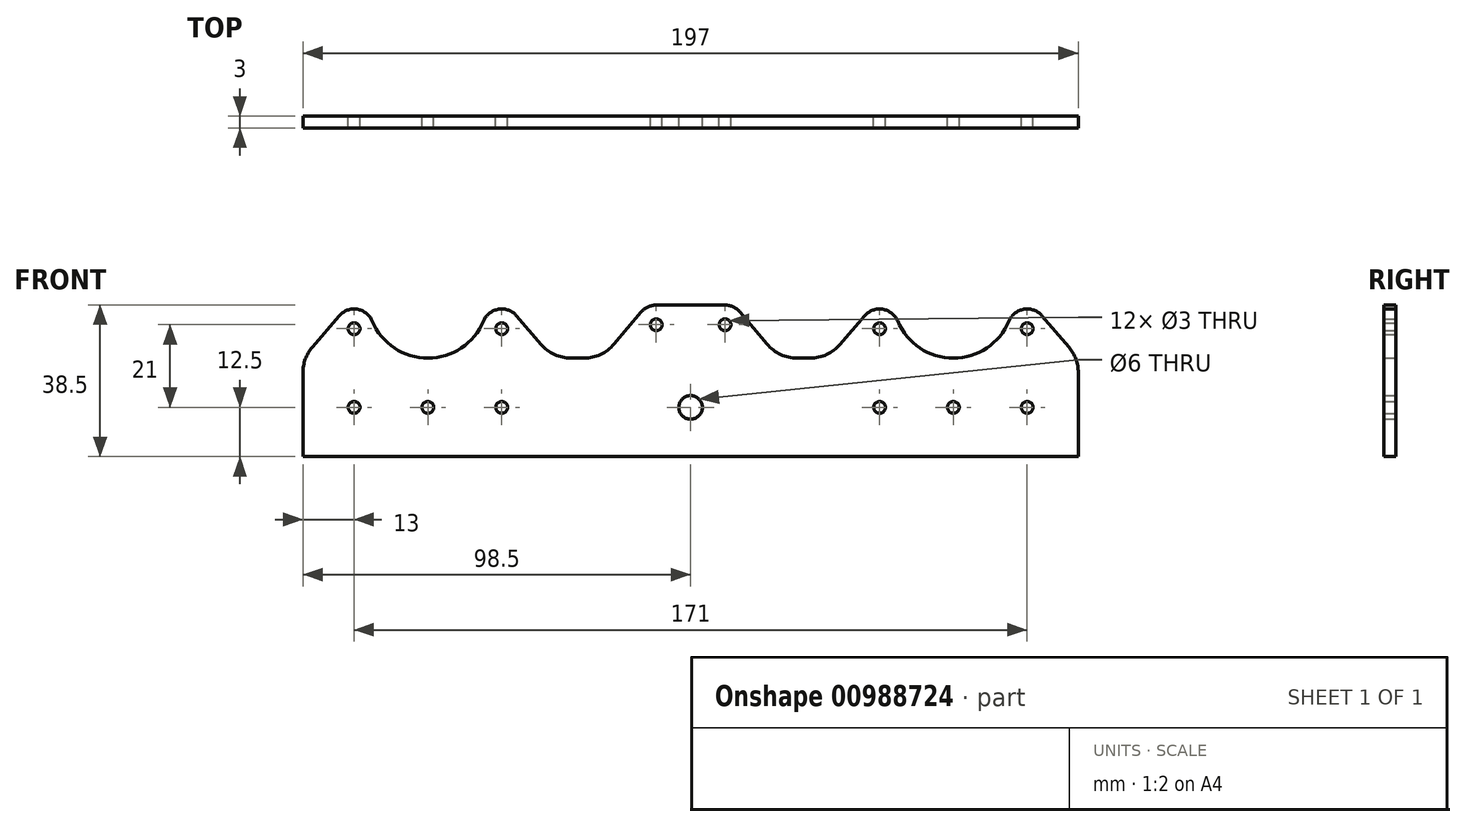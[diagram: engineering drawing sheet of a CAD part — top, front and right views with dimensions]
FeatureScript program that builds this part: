
annotation { "Feature Type Name" : "Feature", "Feature Type Description" : "" }
export const myFeature = defineFeature(function(context is Context, id is Id, definition is map)
    precondition{}
    {
        {
            var Q0;
            Q0=qCreatedBy(makeId("Front.planeOp"),FACE);
            var sketch = newSketch(context, id + "F0", { "sketchPlane" : qUnion([Q0])});
            skLineSegment(sketch, "E0.bottom", {"start": v(0, 0) * mm, "end": v(-197, 0) * mm});
            skLineSegment(sketch, "E0.top", {"start": v(0, 25) * mm, "end": v(-197, 25) * mm});
            skLineSegment(sketch, "E0.left", {"start": v(0, 0) * mm, "end": v(0, 25) * mm});
            skLineSegment(sketch, "E0.right", {"start": v(-197, 0) * mm, "end": v(-197, 25) * mm});
            skCircle(sketch, "E1", {"center": v(-13, 12.5) * mm, "radius": 1.5 * mm});
            skLineSegment(sketch, "E2", {"start": v(-197, 12.5) * mm, "end": v(0, 12.5) * mm, "construction": true});
            skCircle(sketch, "E3", {"center": v(-184, 12.5) * mm, "radius": 1.5 * mm});
            skCircle(sketch, "E4", {"center": v(-165.25, 12.5) * mm, "radius": 1.5 * mm});
            skCircle(sketch, "E5", {"center": v(-146.5, 12.5) * mm, "radius": 1.5 * mm});
            skCircle(sketch, "E6", {"center": v(-98.5, 12.5) * mm, "radius": 3 * mm});
            skCircle(sketch, "E7", {"center": v(-50.5, 12.5) * mm, "radius": 1.5 * mm});
            skCircle(sketch, "E8", {"center": v(-31.75, 12.5) * mm, "radius": 1.5 * mm});
            skCircle(sketch, "E9", {"center": v(-184, 12.5) * mm, "radius": 10 * mm, "construction": true});
            skCircle(sketch, "E10", {"center": v(-146.5, 12.5) * mm, "radius": 10 * mm, "construction": true});
            skCircle(sketch, "E11", {"center": v(-165.25, 12.5) * mm, "radius": 5.75 * mm, "construction": true});
            skCircle(sketch, "E12", {"center": v(-98.5, 12.5) * mm, "radius": 35 * mm, "construction": true});
            skCircle(sketch, "E13", {"center": v(-50.5, 12.5) * mm, "radius": 10 * mm, "construction": true});
            skCircle(sketch, "E14", {"center": v(-13, 12.5) * mm, "radius": 10 * mm, "construction": true});
            skCircle(sketch, "E15", {"center": v(-31.75, 12.5) * mm, "radius": 5.75 * mm, "construction": true});
            skCircle(sketch, "E16", {"center": v(-184, 32.5) * mm, "radius": 1.5 * mm});
            skCircle(sketch, "E17", {"center": v(-146.5, 32.5) * mm, "radius": 1.5 * mm});
            skCircle(sketch, "E18", {"center": v(-50.5, 32.5) * mm, "radius": 1.5 * mm});
            skCircle(sketch, "E19", {"center": v(-13, 32.5) * mm, "radius": 1.5 * mm});
            skLineSegment(sketch, "E20", {"start": v(0, 25) * mm, "end": v(-9.2, 35.75) * mm});
            skArc(sketch, "E21", {"start": v(-9.2, 35.75) * mm, "mid": v(-13.78, 37.44) * mm, "end": v(-17.62, 34.42) * mm});
            skArc(sketch, "E22", {"start": v(-45.88, 34.42) * mm, "mid": v(-49.72, 37.44) * mm, "end": v(-54.3, 35.75) * mm});
            skLineSegment(sketch, "E23", {"start": v(-54.3, 35.75) * mm, "end": v(-63.5, 25) * mm});
            skArc(sketch, "E24", {"start": v(-45.88, 34.42) * mm, "mid": v(-31.75, 25) * mm, "end": v(-17.62, 34.42) * mm});
            skLineSegment(sketch, "E25", {"start": v(-98.5, 0) * mm, "end": v(-98.5, 25) * mm, "construction": true});
            skArc(sketch, "E26.1.0.0", {"start": v(-179.38, 34.42) * mm, "mid": v(-165.25, 25) * mm, "end": v(-151.12, 34.42) * mm});
            skArc(sketch, "E26.1.0.1", {"start": v(-179.38, 34.42) * mm, "mid": v(-183.22, 37.44) * mm, "end": v(-187.8, 35.75) * mm});
            skLineSegment(sketch, "E26.1.0.2", {"start": v(-187.8, 35.75) * mm, "end": v(-197, 25) * mm});
            skLineSegment(sketch, "E26.1.0.3", {"start": v(-133.5, 25) * mm, "end": v(-142.7, 35.75) * mm});
            skArc(sketch, "E26.1.0.4", {"start": v(-142.7, 35.75) * mm, "mid": v(-147.28, 37.44) * mm, "end": v(-151.12, 34.42) * mm});
            skLineSegment(sketch, "E26.direction1", {"start": v(-45.88, 34.42) * mm, "end": v(-179.38, 34.42) * mm, "construction": true});
            skLineSegment(sketch, "E27", {"start": v(-98.5, 12.5) * mm, "end": v(-98.5, 33.5) * mm, "construction": true});
            skLineSegment(sketch, "E28", {"start": v(-107.25, 33.5) * mm, "end": v(-89.75, 33.5) * mm, "construction": true});
            skCircle(sketch, "E29", {"center": v(-107.25, 33.5) * mm, "radius": 1.5 * mm});
            skCircle(sketch, "E30", {"center": v(-89.75, 33.5) * mm, "radius": 1.5 * mm});
            skArc(sketch, "E31", {"start": v(-107.25, 38.5) * mm, "mid": v(-109.36, 38.03) * mm, "end": v(-111.08, 36.71) * mm});
            skArc(sketch, "E32", {"start": v(-85.92, 36.71) * mm, "mid": v(-87.64, 38.03) * mm, "end": v(-89.75, 38.5) * mm});
            skLineSegment(sketch, "E33", {"start": v(-107.25, 38.5) * mm, "end": v(-89.75, 38.5) * mm});
            skLineSegment(sketch, "E34", {"start": v(-85.92, 36.71) * mm, "end": v(-76.1, 25) * mm});
            skLineSegment(sketch, "E35", {"start": v(-111.08, 36.71) * mm, "end": v(-120.9, 25) * mm});
            skSolve(sketch);
        }
        {
            var Q0;
            Q0=makeQuery(id+"F0.imprint","IMPRINT",FACE,{"disambiguationData":[TD([[makeQuery(id+"F0.imprint","IMPRINT",EDGE,{"derivedFrom":sQuery(id+"F0.wireOp",EDGE,"E0.bottom")}),-1.0]])]});
            var Q1;
            Q1=makeQuery(id+"F0.imprint","IMPRINT",FACE,{"disambiguationData":[TD([[makeQuery(id+"F0.imprint","IMPRINT",EDGE,{"derivedFrom":sQuery(id+"F0.wireOp",EDGE,"E18")}),-1.0]])]});
            var Q2;
            {var subQ0=sQuery(id+"F0.wireOp",EDGE,"A3huXqgn-odZi-QKHd-XIsC-R8iYggHlKZpN");Q2=makeQuery(id+"F0.imprint","IMPRINT",FACE,{"disambiguationData":[TD([[makeQuery(id+"F0.imprint","IMPRINT",EDGE,{"derivedFrom":subQ0}),-1.0]])]});}
            var Q3;
            Q3=makeQuery(id+"F0.imprint","IMPRINT",FACE,{"disambiguationData":[TD([[makeQuery(id+"F0.imprint","IMPRINT",EDGE,{"derivedFrom":sQuery(id+"F0.wireOp",EDGE,"E19")}),-1.0]])]});
            var Q4;
            Q4=makeQuery(id+"F0.imprint","IMPRINT",FACE,{"disambiguationData":[TD([[makeQuery(id+"F0.imprint","IMPRINT",EDGE,{"derivedFrom":sQuery(id+"F0.wireOp",EDGE,"E16")}),-1.0]])]});
            var Q5;
            Q5=makeQuery(id+"F0.imprint","IMPRINT",FACE,{"disambiguationData":[TD([[makeQuery(id+"F0.imprint","IMPRINT",EDGE,{"derivedFrom":sQuery(id+"F0.wireOp",EDGE,"E17")}),-1.0]])]});
            var Q6;
            Q6=makeQuery(id+"F0.imprint","IMPRINT",FACE,{"disambiguationData":[TD([[makeQuery(id+"F0.imprint","IMPRINT",EDGE,{"derivedFrom":sQuery(id+"F0.wireOp",EDGE,"E29")}),-1.0]])]});
            extrude(context, id + "F1", {"entities" : qUnion([Q0, Q1, Q2, Q3, Q4, Q5, Q6]), "depth" : 3 * mm, "offsetDistance" : 25 * mm});
        }
        {
            var Q0;
            Q0=makeQuery(id+"F1.opExtrude","SWEPT_EDGE",EDGE,{"disambiguationData":[OSD([sQuery(id+"F0.wireOp",EDGE,"E0.top"),sQuery(id+"F0.wireOp",EDGE,"E0.left"),sQuery(id+"F0.wireOp",EDGE,"E20")])]});
            var Q1;
            Q1=makeQuery(id+"F1.opExtrude","SWEPT_EDGE",EDGE,{"disambiguationData":[OSD([sQuery(id+"F0.wireOp",EDGE,"E0.top"),sQuery(id+"F0.wireOp",EDGE,"E0.right"),sQuery(id+"F0.wireOp",EDGE,"E26.1.0.2")])]});
            var Q2;
            Q2=makeQuery(id+"F1.opExtrude","SWEPT_EDGE",EDGE,{"disambiguationData":[OSD([sQuery(id+"F0.wireOp",EDGE,"E0.top"),sQuery(id+"F0.wireOp",EDGE,"E26.1.0.3")])]});
            var Q3;
            Q3=makeQuery(id+"F1.opExtrude","SWEPT_EDGE",EDGE,{"disambiguationData":[OSD([sQuery(id+"F0.wireOp",EDGE,"E0.top"),sQuery(id+"F0.wireOp",EDGE,"E23")])]});
            var Q4;
            Q4=makeQuery(id+"F1.opExtrude","SWEPT_EDGE",EDGE,{"disambiguationData":[OSD([sQuery(id+"F0.wireOp",EDGE,"E0.top"),sQuery(id+"F0.wireOp",EDGE,"E35")])]});
            var Q5;
            Q5=makeQuery(id+"F1.opExtrude","SWEPT_EDGE",EDGE,{"disambiguationData":[OSD([sQuery(id+"F0.wireOp",EDGE,"E0.top"),sQuery(id+"F0.wireOp",EDGE,"E34")])]});
            fillet(context, id + "F2", {"entities" : qUnion([Q0, Q1, Q2, Q3, Q4, Q5]), "radius" : 10 * mm, "tangentPropagation" : true, "allowEdgeOverflow" : false});
        }
    });
